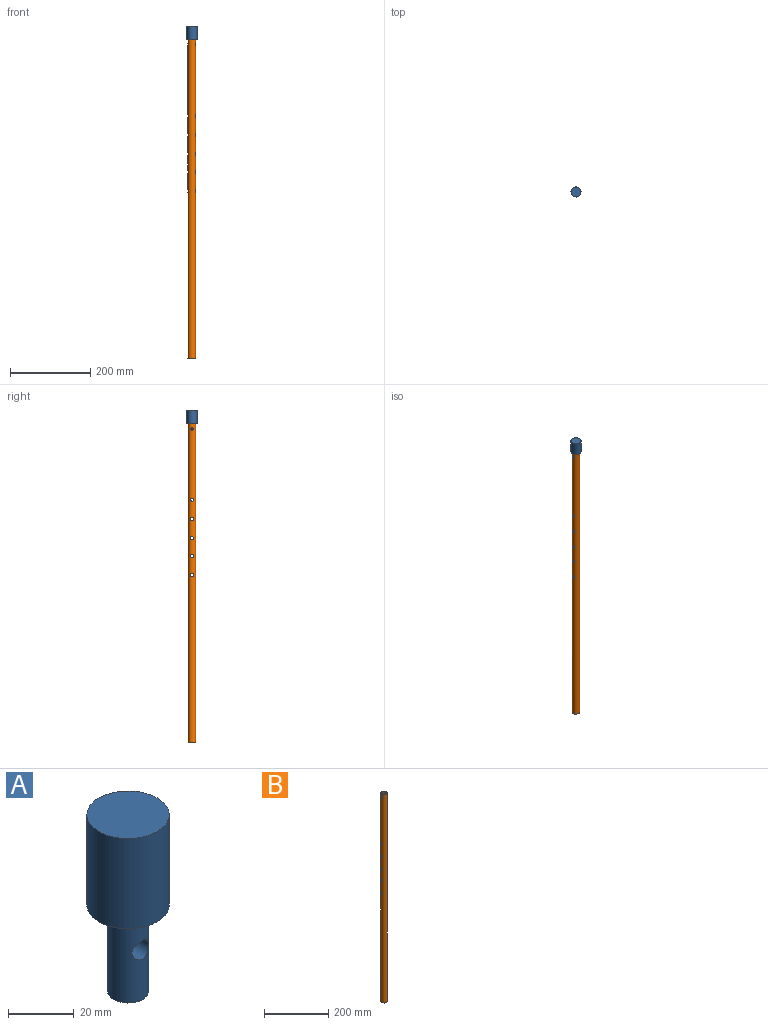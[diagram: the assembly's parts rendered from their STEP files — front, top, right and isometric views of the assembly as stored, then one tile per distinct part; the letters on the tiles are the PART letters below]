
ASSEMBLY  parts=2 mates=1
PART A: 6 faces, bbox 25x25x65.5 mm
  f0: cylinder r=12.5mm len=33.5mm, axis (0,0,1), area 2631.1mm2, adj f1,f2
  f1: plane 25x25mm, normal (0,0,-1), area 368.2mm2, adj f0,f3
  f2: plane 25x25mm, normal (0,0,1), area 490.9mm2, adj f0
  f3: cylinder r=6.25mm len=32mm, axis (0,0,1), area 1176.2mm2, adj f1,f4,f5
  f4: plane 12.5x12.5mm, normal (0,0,-1), area 122.7mm2, adj f3
  f5: cylinder r=3.5mm len=12.5mm, axis (0,-1,0), area 251.9mm2, adj f3
PART B: 16 faces, bbox 19x19x795 mm
  f0: cylinder r=3mm len=6mm, axis (-1,0,0), area 58.8mm2, adj f6,f15
  f1: cylinder r=4mm len=8mm, axis (1,0,0), area 81.2mm2, adj f6,f15
  f2: cylinder r=4mm len=8mm, axis (1,0,0), area 81.2mm2, adj f6,f15
  f3: cylinder r=4mm len=8mm, axis (1,0,0), area 81.2mm2, adj f6,f15
  f4: cylinder r=4mm len=8mm, axis (1,0,0), area 81.2mm2, adj f6,f15
  f5: cylinder r=4mm len=8mm, axis (1,0,0), area 81.2mm2, adj f6,f15
  f6: cylinder r=9.5mm len=795mm, axis (0,0,-1), area 46881.8mm2, adj f0,f1,f2,f3,f4,f5,f7,f8
  f7: plane 19x19mm, normal (0,0,1), area 150.8mm2, adj f6,f15
  f8: plane 19x19mm, normal (0,0,-1), area 150.8mm2, adj f6,f15
  f9: cylinder r=3mm len=6mm, axis (-1,0,0), area 58.8mm2, adj f6,f15
  f10: cylinder r=4mm len=8mm, axis (1,0,0), area 81.2mm2, adj f6,f15
  f11: cylinder r=4mm len=8mm, axis (1,0,0), area 81.2mm2, adj f6,f15
  f12: cylinder r=4mm len=8mm, axis (1,0,0), area 81.2mm2, adj f6,f15
  f13: cylinder r=4mm len=8mm, axis (1,0,0), area 81.2mm2, adj f6,f15
  f14: cylinder r=4mm len=8mm, axis (1,0,0), area 81.2mm2, adj f6,f15
  f15: cylinder r=6.5mm len=795mm, axis (0,0,1), area 31879.5mm2, adj f0,f1,f2,f3,f4,f5,f7,f8
PLACE A rot(axis=(0,0,-1),90deg) t=(257.98,-28.6,165.69)mm
PLACE B t=(257.39,-28.6,-663.31)mm
MATE fastened A.f5 <-> B.f0  axis (-1,0,0) through (251.65,-28.6,118.69)mm
